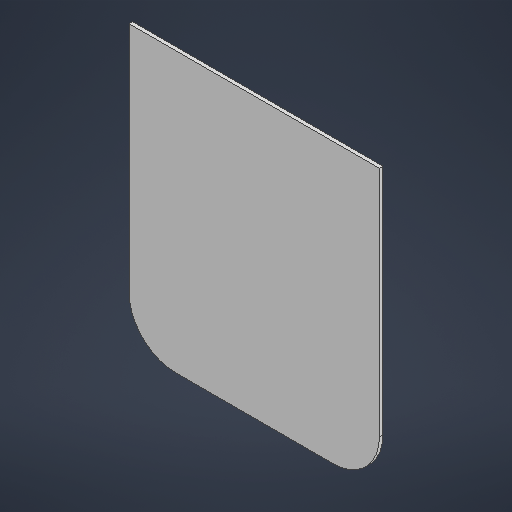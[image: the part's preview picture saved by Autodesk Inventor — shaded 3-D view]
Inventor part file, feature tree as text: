
AUTODESK INVENTOR PART (.ipt)
format: ipt  version: 2025 (Build 290162000, 162)  size: 170,496 bytes
history: native  units: mm
features: extrude x1, fillet x1, sketch x1
ambient origin geometry x8: Origin, YZ Plane, XZ Plane, XY Plane, X Axis, Y Axis, Z Axis, Center Point
bodies: 实体1 (feature_tree)
feature tree (3):
  extrude  "拉伸1"  Depth=78.0mm
  fillet  "圆角1"  Radius=1.0mm
  sketch  "草图1"  dims[d0=70.0mm d1=78.0mm d2=1.0mm d3=0.0mm d4=13.0mm]
